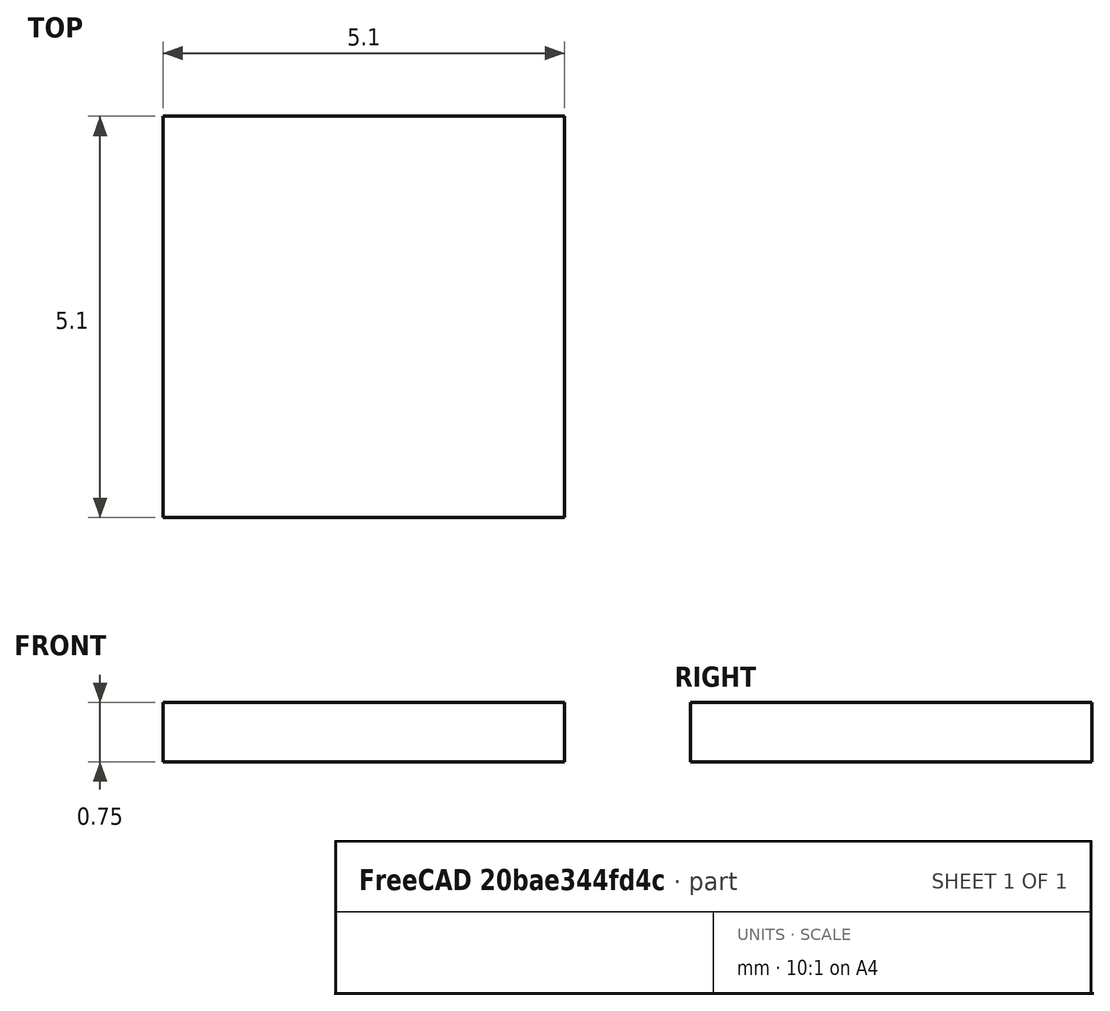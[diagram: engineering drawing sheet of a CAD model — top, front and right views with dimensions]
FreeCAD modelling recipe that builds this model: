
FCSTD DOCUMENT  (FreeCAD 0.21R33668 +26 (Git))
Label: HMV080_Optical_Cover_5x5x0.7mm
License: All rights reserved
LicenseURL: http://en.wikipedia.org/wiki/All_rights_reserved
objects: Sketcher::SketchObject×1, PartDesign::Pad×1, PartDesign::Body×1
note: 4 computed .brp shape members not serialized (recipe doc carries the construction recipe); baked Part::Feature solids carry a one-line shape summary decoded from their .brp

FEATURE [Sketcher::SketchObject] Sketch
  FullyConstrained = true
  MapMode = 5
  Support = -> [XY_Plane]
  sketch-geometry (5):
    g0: LineSegment StartX=2.55 StartY=-2.55 StartZ=0 EndX=2.55 EndY=2.55 EndZ=0
    g1: LineSegment StartX=2.55 StartY=2.55 StartZ=0 EndX=-2.55 EndY=2.55 EndZ=0
    g2: LineSegment StartX=-2.55 StartY=2.55 StartZ=0 EndX=-2.55 EndY=-2.55 EndZ=0
    g3: LineSegment StartX=-2.55 StartY=-2.55 StartZ=0 EndX=2.55 EndY=-2.55 EndZ=0
    g4: GeomPoint X=0 Y=0 Z=0
  constraints (12):
    c: Coincident(g0,g1)
    c: Coincident(g1,g2)
    c: Coincident(g2,g3)
    c: Coincident(g3,g0)
    c: Horizontal(g1)
    c: Horizontal(g3)
    c: Vertical(g0)
    c: Vertical(g2)
    c: Symmetric(g1,g0,g4)
    c: Coincident(g4,g-1)
    c: DistanceX(g1,g1) = 5.1
    c: DistanceY(g0,g0) = 5.1
FEATURE [PartDesign::Pad] Pad
  Direction = (0,0,1)
  Length = 0.75
  Length2 = 10
  Profile = -> Sketch
  ReferenceAxis = -> Sketch [N_Axis]
  Type = 0
FEATURE [PartDesign::Body] Body
  Group = -> [Sketch,Pad]
  Origin = -> Origin
  Tip = -> Pad
